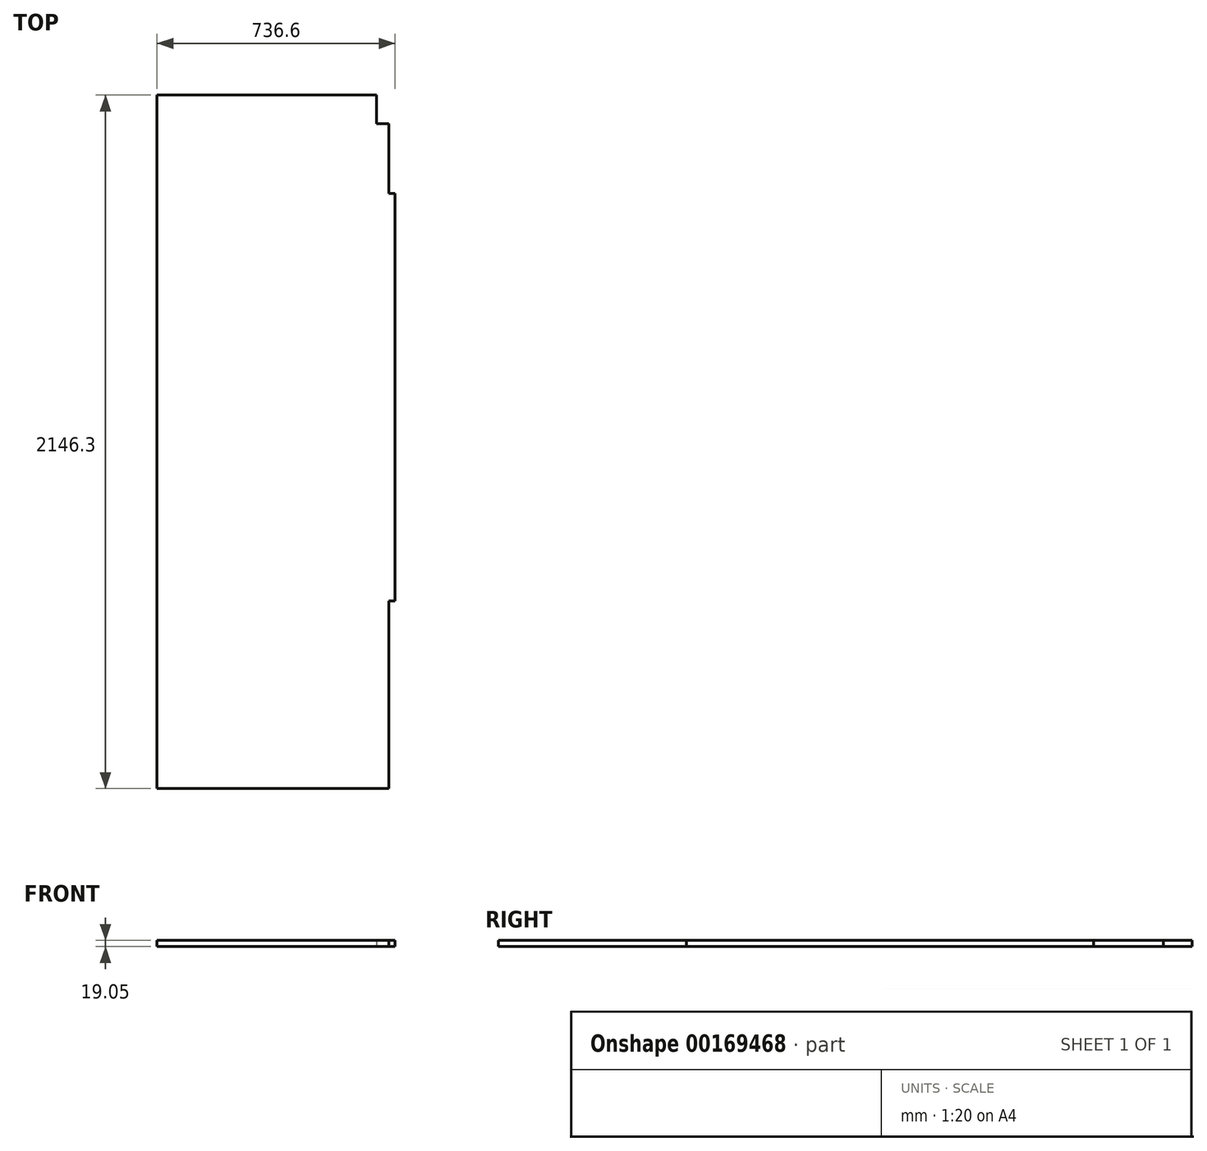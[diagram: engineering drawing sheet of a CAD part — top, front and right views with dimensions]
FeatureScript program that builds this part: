
annotation { "Feature Type Name" : "Feature", "Feature Type Description" : "" }
export const myFeature = defineFeature(function(context is Context, id is Id, definition is map)
    precondition{}
    {
        {
            var Q0;
            Q0=qCreatedBy(makeId("Top.planeOp"),FACE);
            var sketch = newSketch(context, id + "F0", { "sketchPlane" : qUnion([Q0])});
            skLineSegment(sketch, "E0", {"start": v(40.11, 675.93) * mm, "end": v(719.56, 675.93) * mm});
            skLineSegment(sketch, "E1", {"start": v(776.71, 371.13) * mm, "end": v(776.71, -889.35) * mm});
            skLineSegment(sketch, "E2", {"start": v(40.11, -1470.37) * mm, "end": v(40.11, 675.93) * mm});
            skLineSegment(sketch, "E3", {"start": v(757.66, 587.03) * mm, "end": v(757.66, 371.13) * mm});
            skLineSegment(sketch, "E4", {"start": v(757.66, 371.13) * mm, "end": v(776.71, 371.13) * mm});
            skLineSegment(sketch, "E5", {"start": v(776.71, -889.35) * mm, "end": v(757.66, -889.35) * mm});
            skLineSegment(sketch, "E6", {"start": v(757.66, -889.35) * mm, "end": v(757.66, -1470.37) * mm});
            skLineSegment(sketch, "E7", {"start": v(757.66, -1470.37) * mm, "end": v(40.11, -1470.37) * mm});
            skLineSegment(sketch, "E8", {"start": v(757.66, 587.03) * mm, "end": v(719.56, 587.03) * mm});
            skLineSegment(sketch, "E9", {"start": v(719.56, 587.03) * mm, "end": v(719.56, 675.93) * mm});
            skSolve(sketch);
        }
        {
            var Q0;
            Q0 = qSketchRegion(id + "F0", true);
            extrude(context, id + "F1", {"entities" : qUnion([Q0]), "depth" : 19.05 * mm});
        }
    });
